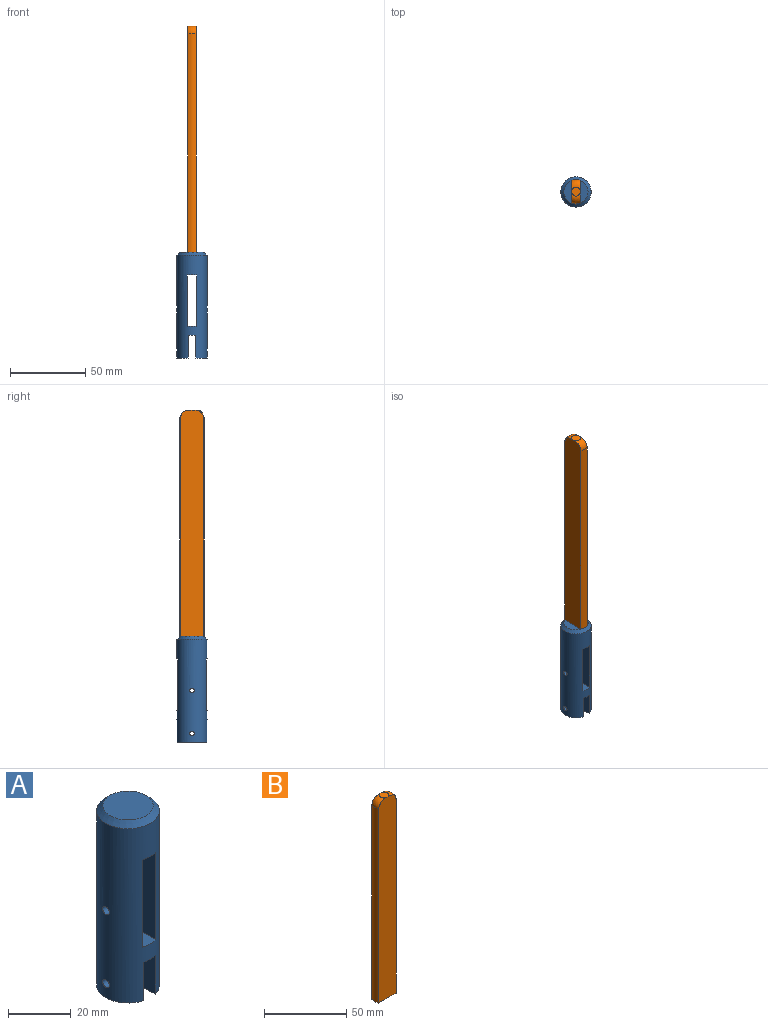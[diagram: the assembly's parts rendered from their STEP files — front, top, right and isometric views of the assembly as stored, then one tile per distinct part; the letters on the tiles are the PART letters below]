
ASSEMBLY  parts=2 mates=1
PART A: 16 faces, bbox 20x20x70 mm
  f0: cylinder r=10mm len=68mm, axis (0,0,-1), area 3678.2mm2, adj f1,f3,f4,f5,f6,f7,f8,f9
  f1: plane 20x5mm, normal (0,0,-1), area 98.9mm2, adj f0,f3,f5
  f2: plane 16x16mm, normal (0,0,1), area 201.1mm2, adj f7
  f3: plane 19.37x15mm, normal (-1,0,0), area 283.4mm2, adj f0,f1,f4,f9
  f4: plane 19.37x7.5mm, normal (0,0,-1), area 107.6mm2, adj f0,f3
  f5: plane 19.37x15mm, normal (1,0,0), area 283.4mm2, adj f0,f1,f6,f8
  f6: plane 19.37x7.5mm, normal (0,0,-1), area 107.6mm2, adj f0,f5
  f7: cone r=8mm half-angle=45deg, axis (0,0,-1), area 159.9mm2, adj f0,f2
  f8: cylinder r=1.5mm len=7.5mm, axis (1,0,0), area 70.2mm2, adj f0,f5
  f9: cylinder r=1.5mm len=7.5mm, axis (1,0,0), area 70.2mm2, adj f0,f3
  f10: plane 34x19.08mm, normal (-1,0,0), area 641.6mm2, adj f0,f11,f13,f15
  f11: plane 20x6mm, normal (0,0,-1), area 118.2mm2, adj f0,f10,f12
  f12: plane 34x19.08mm, normal (1,0,0), area 641.6mm2, adj f0,f11,f13,f14
  f13: plane 20x6mm, normal (0,0,1), area 118.2mm2, adj f0,f10,f12
  f14: cylinder r=1.5mm len=7mm, axis (1,0,0), area 65.4mm2, adj f0,f12
  f15: cylinder r=1.5mm len=7mm, axis (1,0,0), area 65.4mm2, adj f0,f10
PART B: 8 faces, bbox 16x15.5x150 mm
  f0: plane 150x14.9mm, normal (0,-1,0), area 2223.7mm2, adj f1,f3,f4,f5,f6,f7
  f1: cylinder r=8mm len=145mm, axis (0,0,-1), area 863.4mm2, adj f0,f2,f5,f6
  f2: plane 150x14.9mm, normal (0,1,0), area 2223.7mm2, adj f1,f3,f4,f5,f6,f7
  f3: cylinder r=8mm len=145mm, axis (0,0,-1), area 863.4mm2, adj f0,f2,f5,f7
  f4: plane 6x5.82mm, normal (0,0,1), area 28.1mm2, adj f0,f2,f6,f7
  f5: plane 16x5.82mm, normal (0,0,-1), area 91mm2, adj f0,f1,f2,f3
  f6: torus R=3mm, axis (0,0,1), area 48.5mm2, adj f0,f1,f2,f4
  f7: torus R=3mm, axis (0,0,1), area 48.5mm2, adj f0,f2,f3,f4
PLACE A t=(-16.37,-0.13,-43.51)mm
PLACE B rot(axis=(0,0,1),90deg) t=(-16.37,-0.13,11.49)mm
MATE fastened B.f1 <-> A.f0  axis (0,0,-1) through (-16.37,-0.13,11.49)mm
